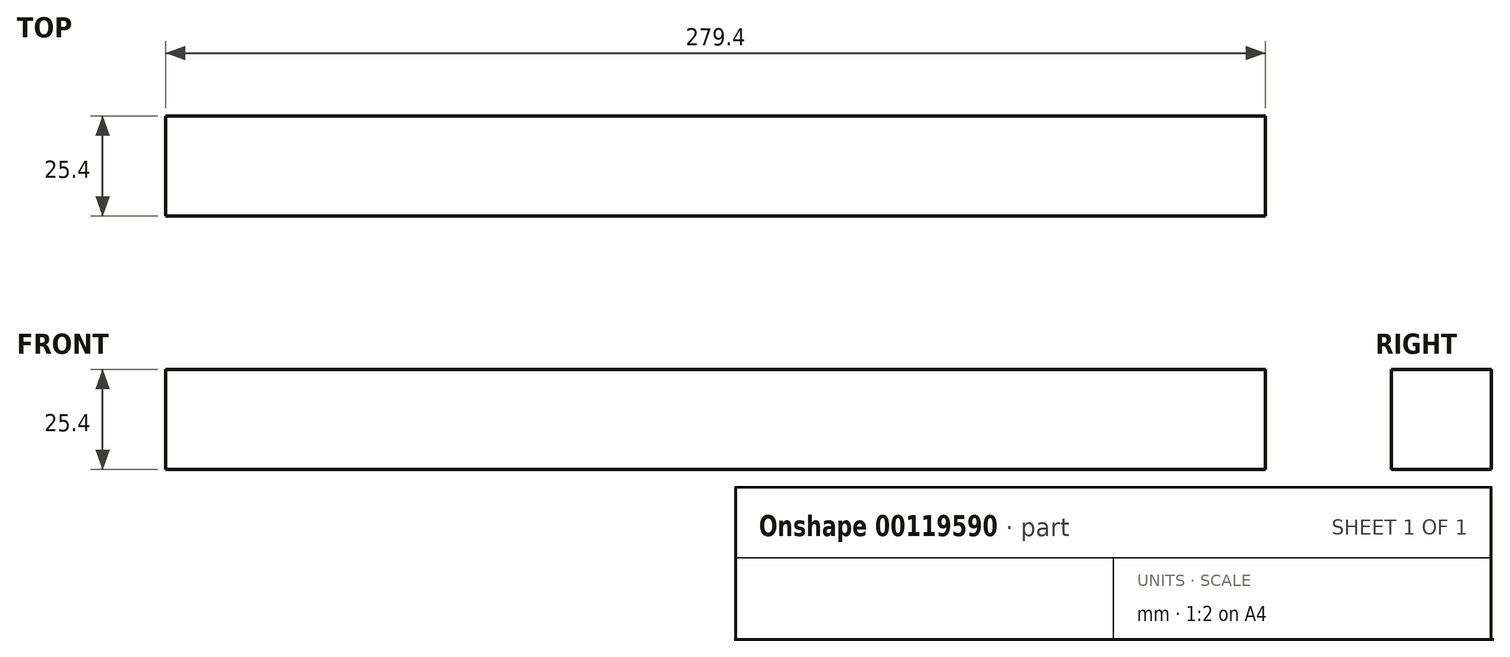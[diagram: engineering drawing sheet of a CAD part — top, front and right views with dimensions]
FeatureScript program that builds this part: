
annotation { "Feature Type Name" : "Feature", "Feature Type Description" : "" }
export const myFeature = defineFeature(function(context is Context, id is Id, definition is map)
    precondition{}
    {
        {
            var Q0;
            Q0=qCreatedBy(makeId("Front.planeOp"),FACE);
            var sketch = newSketch(context, id + "F0", { "sketchPlane" : qUnion([Q0])});
            skLineSegment(sketch, "E0", {"start": v(0, 0) * mm, "end": v(0, 25.4) * mm});
            skLineSegment(sketch, "E1", {"start": v(0, 25.4) * mm, "end": v(279.4, 25.4) * mm});
            skLineSegment(sketch, "E2", {"start": v(279.4, 25.4) * mm, "end": v(279.4, 0) * mm});
            skLineSegment(sketch, "E3", {"start": v(279.4, 0) * mm, "end": v(0, 0) * mm});
            skSolve(sketch);
        }
        {
            var Q0;
            Q0=makeQuery(id+"F0.imprint","IMPRINT",FACE,{"disambiguationData":[TD([[makeQuery(id+"F0.imprint","IMPRINT",EDGE,{"derivedFrom":sQuery(id+"F0.wireOp",EDGE,"E0")}),-1.0]])]});
            extrude(context, id + "F1", {"entities" : qUnion([Q0]), "depth" : 25.4 * mm});
        }
    });
